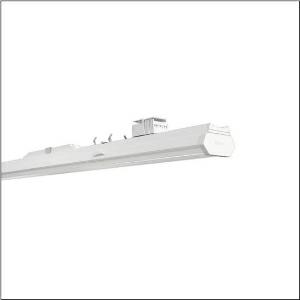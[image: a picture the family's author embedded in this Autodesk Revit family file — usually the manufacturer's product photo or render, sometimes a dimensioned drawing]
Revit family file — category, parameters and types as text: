
# Revit family: licross_r__11_protected_mo_51ts11vn465f_4959
name_source: partatom
category: Lighting Fixtures
units: mm (PartAtom-declared; Revit-internal decimal feet)

## family parameters
Cut with Voids When Loaded = No
Host = Face
Light Source = No
Part Type = Normal
Room Calculation Point = No
Round Connector Dimension = Use Diameter
Shared = No

## types (1)
- --- (1 x LED, 6910 lm, 42.6 W, 4000K)
    Apparent Load = 43 VA
    CIE Flux Codes = 83 94 98 100 100
    Color Rendering = 80
    Color Temperature = 4000K
    Default Elevation = 1800 mm
    Description = Licross® 11 Protected MO, luminaire insert, of sheet steel, galvanised, coil coated, white, length: 1.500mm, width: 90mm, height: 101mm, LED rated luminous flux: 6.910lm, light colour: 840, control gear: DALI 2, CLO, control gear: ECG DALI, with plug, 5-pole, with phase selection, mains connection: 220..240V, AC, 50/60Hz, halogen-free wiring, primary optical cover: cover, of PMMA, light emission: direct with ceiling illumination distribution, protection rating (complete): IP50, insulation class (complete): insulation class I (protective earthing), certification: CE, ENEC, VDE, UKCA, protection symbol: D if used in an environment with non-conductive dust loads with corresponding accessories, permissible ambient temperature for indoor applications: -25..+40°C, corresponds to IFS (International Featured Standards) requirements for safety and quality in the food industry, reducing of maximum allowable ambient temperature of 5°C with ceiling mounting, packaging unit: 1 piece
    Height = 92 mm
    Lamp = 1 x LED
    Lamp Light Flux = 6910 lm
    Lamp Power = 42.6 W
    Lamp count = 1
    Length = 1500 mm
    Luminous efficacy = 162 lm/W
    Manufacturer = Siteco
    ModVariant = No
    Model = 51TS11VN465F
    Mounting Place = Ceiling
    Mounting Type = Pendant
    Number of Poles = 1
    OnlyDefault = Yes
    Power Factor = 1
    Product Name = Licross® 11 Protected MO
    Product group = luminaire insert
    ProductGroupID = 902
    Protection Class = Protection class I
    Protection Degree = IP 50
    RLX_Detail_Level = 1
    RlxData = <blob elided: 24005 chars, md5=60ae4b1b>
    Socket = socket
    Standby Power = 0 W
    System Light Flux = 6910 lm
    System Power = 43 W
    Type Comments = factory setting: luminous flux: 100 % | dim-lin: 254 | 280 mA
    Type Image = l_1256145.jpg
    URL = http://relux.com
    VarID = @adj_128579
    Voltage = 0 V
    Weight = 0.00 kg
    Width = 88 mm

## geometry (parser evidence)
native form markers: Blend x4, Sweep x13
no freeform markers — native parametric forms only
